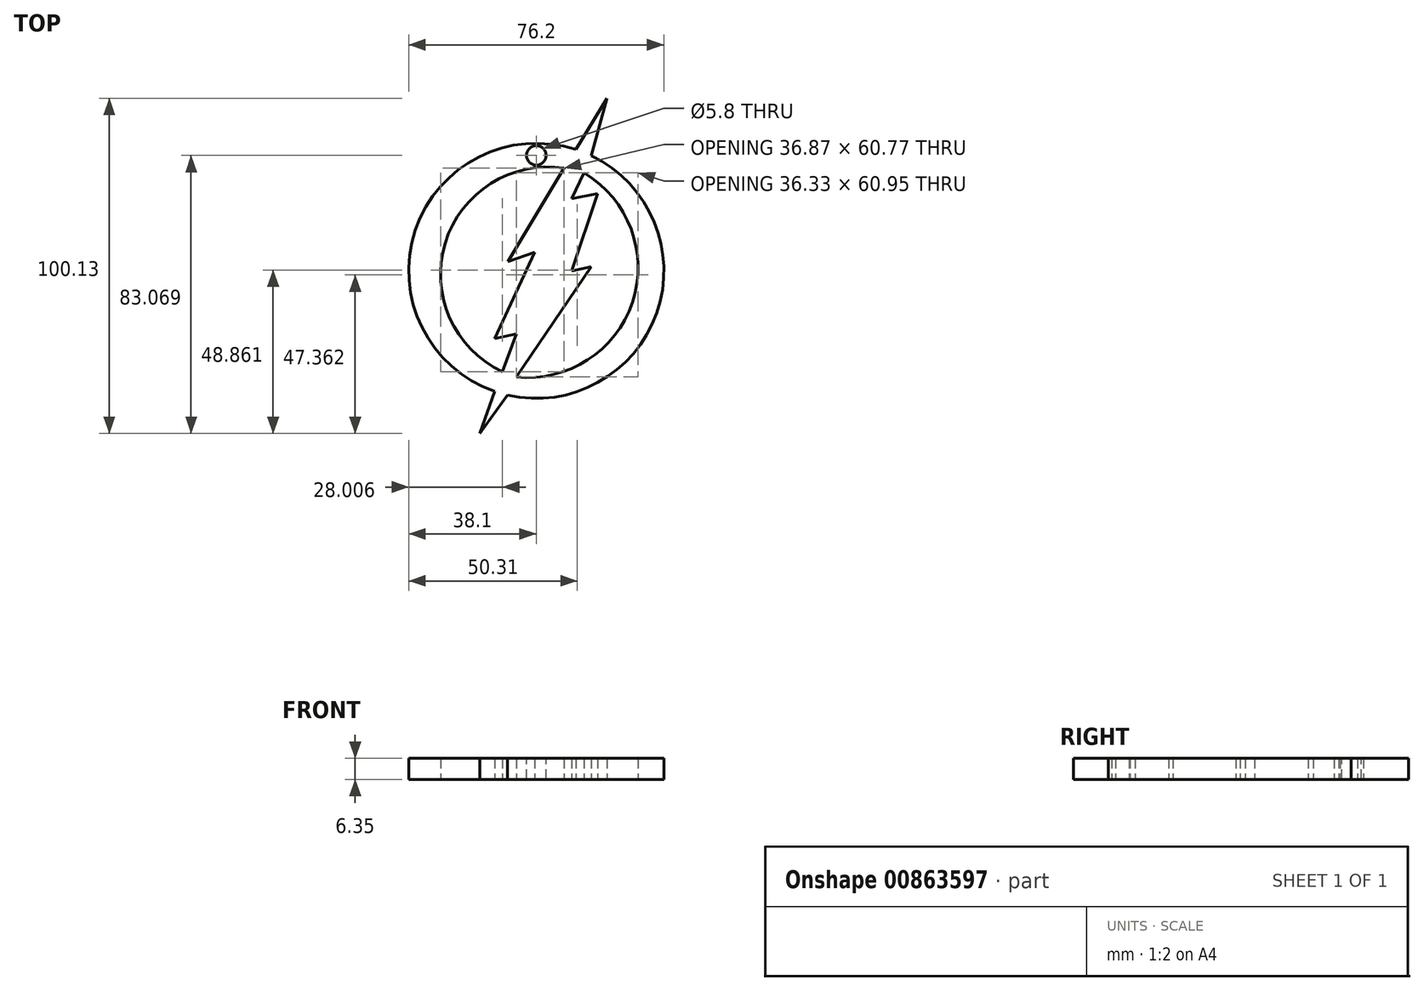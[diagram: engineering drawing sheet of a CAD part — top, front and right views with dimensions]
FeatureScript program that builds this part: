
annotation { "Feature Type Name" : "Feature", "Feature Type Description" : "" }
export const myFeature = defineFeature(function(context is Context, id is Id, definition is map)
    precondition{}
    {
        {
            var Q0;
            Q0=qCreatedBy(makeId("Top.planeOp"),FACE);
            var sketch = newSketch(context, id + "F0", { "sketchPlane" : qUnion([Q0])});
            skLineSegment(sketch, "E0", {"start": v(21.06, 51.55) * mm, "end": v(11.72, 36.08) * mm});
            skLineSegment(sketch, "E1", {"start": v(21.06, 51.55) * mm, "end": v(16.4, 34.21) * mm});
            skPoint(sketch, "E1.endSnap0", {"position": v(16.4, 43.81) * mm});
            skLineSegment(sketch, "E2", {"start": v(18.27, 23.09) * mm, "end": v(10.56, 21.52) * mm});
            skLineSegment(sketch, "E3", {"start": v(10.56, 0) * mm, "end": v(18.27, 23.09) * mm});
            skLineSegment(sketch, "E4", {"start": v(10.56, 0) * mm, "end": v(16.4, 1.18) * mm});
            skLineSegment(sketch, "E5", {"start": v(-8.49, -36.97) * mm, "end": v(-16.9, -48.58) * mm});
            skLineSegment(sketch, "E6", {"start": v(-16.9, -48.58) * mm, "end": v(-12.35, -35.87) * mm});
            skLineSegment(sketch, "E7", {"start": v(-10.18, -30.1) * mm, "end": v(-5.96, -18.89) * mm});
            skLineSegment(sketch, "E8", {"start": v(-5.96, -18.89) * mm, "end": v(-12.35, -20.18) * mm});
            skLineSegment(sketch, "E9", {"start": v(-12.35, -20.18) * mm, "end": v(-0.54, 5.54) * mm});
            skLineSegment(sketch, "E10", {"start": v(-0.54, 5.54) * mm, "end": v(-8.49, 2.77) * mm});
            skLineSegment(sketch, "E11", {"start": v(-8.49, 2.77) * mm, "end": v(8.34, 30.66) * mm});
            skArc(sketch, "E12", {"start": v(11.81, 36.22) * mm, "mid": v(-36.12, 12.11) * mm, "end": v(-12.4, -36.02) * mm});
            skArc(sketch, "E13", {"start": v(8.34, 30.66) * mm, "mid": v(-27.2, 8.29) * mm, "end": v(-10.18, -30.1) * mm});
            skArc(sketch, "E14.trimOffspring", {"start": v(-8.6, -37.12) * mm, "mid": v(35.96, -12.59) * mm, "end": v(16.43, 34.37) * mm});
            skLineSegment(sketch, "E15", {"start": v(10.56, 21.52) * mm, "end": v(14.3, 29.26) * mm});
            skLineSegment(sketch, "E16", {"start": v(-5.96, -31.7) * mm, "end": v(16.4, 1.18) * mm});
            skArc(sketch, "E17", {"start": v(-5.96, -31.7) * mm, "mid": v(28.7, -9.37) * mm, "end": v(14.3, 29.26) * mm});
            skSolve(sketch);
        }
        {
            var Q0;
            Q0=makeQuery(id+"F0.imprint","IMPRINT",FACE,{"disambiguationData":[TD([[makeQuery(id+"F0.imprint","IMPRINT",EDGE,{"derivedFrom":sQuery(id+"F0.wireOp",EDGE,"kDMsdJSV-2mQ8-LJaS-euuK-oHCO8Yye3mz4")}),1.0]])]});
            var Q1;
            Q1=makeQuery(id+"F0.imprint","IMPRINT",FACE,{"disambiguationData":[TD([[makeQuery(id+"F0.imprint","IMPRINT",EDGE,{"derivedFrom":sQuery(id+"F0.wireOp",EDGE,"HiK4emQD-gUYz-Ytqw-OSLd-Uxtfr9rCMUka")}),1.0]])]});
            var Q2;
            {var subQ0=sQuery(id+"F0.wireOp",EDGE,"E6");var subQ1=sQuery(id+"F0.wireOp",EDGE,"E5");var subQ2=makeQuery(id+"F0.imprint","INTERSECT",VERTEX,{"derivedFrom":[subQ1,subQ0]});Q2=makeQuery(id+"F0.imprint","IMPRINT",FACE,{"disambiguationData":[TD([[makeQuery(id+"F0.imprint","IMPRINT",EDGE,{"disambiguationData":[TD([[subQ2,1.0]])],"derivedFrom":subQ1}),-1.0]])]});}
            var Q3;
            {var subQ0=sQuery(id+"F0.wireOp",EDGE,"E1");var subQ1=sQuery(id+"F0.wireOp",EDGE,"E0");var subQ2=makeQuery(id+"F0.imprint","INTERSECT",VERTEX,{"derivedFrom":[subQ1,subQ0]});Q3=makeQuery(id+"F0.imprint","IMPRINT",FACE,{"disambiguationData":[TD([[makeQuery(id+"F0.imprint","IMPRINT",EDGE,{"disambiguationData":[TD([[subQ2,-1.0]])],"derivedFrom":subQ1}),1.0]])]});}
            extrude(context, id + "F1", {"entities" : qUnion([Q0, Q1, Q2, Q3]), "depth" : 6.35 * mm, "offsetDistance" : 25.4 * mm});
        }
        {
            var Q0;
            Q0=makeQuery(id+"F1.opExtrude","CAP_FACE",FACE,{"disambiguationData":[OSD([sQuery(id+"F0.wireOp",EDGE,"E0"),sQuery(id+"F0.wireOp",EDGE,"E1"),sQuery(id+"F0.wireOp",EDGE,"HiK4emQD-gUYz-Ytqw-OSLd-Uxtfr9rCMUka"),sQuery(id+"F0.wireOp",EDGE,"E2"),sQuery(id+"F0.wireOp",EDGE,"E3"),sQuery(id+"F0.wireOp",EDGE,"E4"),sQuery(id+"F0.wireOp",EDGE,"owyAgIFF-RVMT-ObYs-UFmp-7Wf7PsS9pBmw"),sQuery(id+"F0.wireOp",EDGE,"E5"),sQuery(id+"F0.wireOp",EDGE,"E6"),sQuery(id+"F0.wireOp",EDGE,"E7"),sQuery(id+"F0.wireOp",EDGE,"E8"),sQuery(id+"F0.wireOp",EDGE,"E9"),sQuery(id+"F0.wireOp",EDGE,"E10"),sQuery(id+"F0.wireOp",EDGE,"E11"),sQuery(id+"F0.wireOp",EDGE,"E12"),sQuery(id+"F0.wireOp",EDGE,"E13"),sQuery(id+"F0.wireOp",EDGE,"p25KZ7Lp-nlZs-HeBO-Etue-g4bSYRPqVeyg"),sQuery(id+"F0.wireOp",EDGE,"E14.trimOffspring")])],"isStart":false});
            var sketch = newSketch(context, id + "F2", { "sketchPlane" : qUnion([Q0])});
            skCircle(sketch, "E18", {"center": v(0, 34.49) * mm, "radius": 2.9 * mm});
            skSolve(sketch);
        }
        {
            var Q0;
            Q0=makeQuery(id+"F2.imprint","IMPRINT",FACE,{"disambiguationData":[TD([[makeQuery(id+"F2.imprint","IMPRINT",EDGE,{"derivedFrom":sQuery(id+"F2.wireOp",EDGE,"E18")}),1.0]])]});
            extrude(context, id + "F3", {"entities" : qUnion([Q0]), "operationType" : NewBodyOperationType.REMOVE, "oppositeDirection" : true, "depth" : 12.7 * mm, "offsetDistance" : 25.4 * mm});
        }
    });
